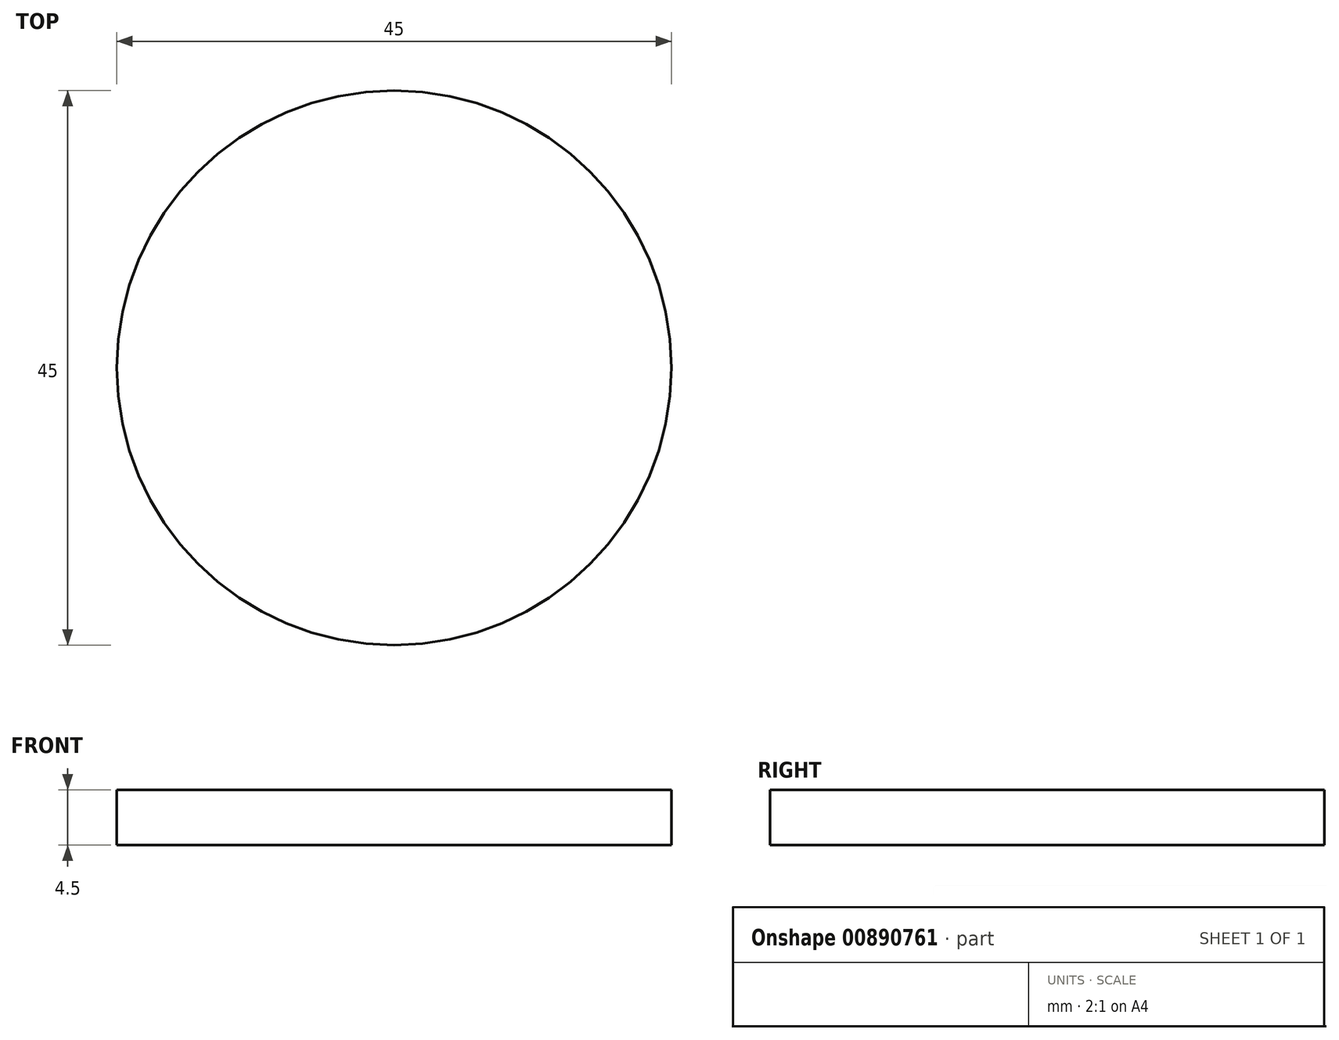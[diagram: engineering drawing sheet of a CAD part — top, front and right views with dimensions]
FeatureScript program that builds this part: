
annotation { "Feature Type Name" : "Feature", "Feature Type Description" : "" }
export const myFeature = defineFeature(function(context is Context, id is Id, definition is map)
    precondition{}
    {
        {
            var Q0;
            Q0=qCreatedBy(makeId("Top.planeOp"),FACE);
            var sketch = newSketch(context, id + "F0", { "sketchPlane" : qUnion([Q0])});
            skCircle(sketch, "E0", {"center": v(0, 0) * mm, "radius": 22.5 * mm});
            skLineSegment(sketch, "E1.left", {"start": v(0, -22.5) * mm, "end": v(0, -20) * mm, "construction": true});
            skLineSegment(sketch, "E2.left", {"start": v(0, -20) * mm, "end": v(0, 26) * mm, "construction": true});
            skEllipse(sketch, "E3", {"center": v(0, 3) * mm, "majorRadius": 23 * mm, "minorRadius": 7 * mm, "majorAxis": v(0, 1)});
            skSolve(sketch);
        }
        {
            var Q0;
            {var subQ0=sQuery(id+"F0.wireOp",EDGE,"E3");var subQ1=sQuery(id+"F0.wireOp",EDGE,"E0");var subQ2=makeQuery(id+"F0.imprint","INTERSECT",VERTEX,{"disambiguationData":[OD(0.0)],"derivedFrom":[subQ1,subQ0]});Q0=makeQuery(id+"F0.imprint","IMPRINT",FACE,{"disambiguationData":[TD([[makeQuery(id+"F0.imprint","IMPRINT",EDGE,{"disambiguationData":[TD([[subQ2,-1.0]])],"derivedFrom":subQ1}),1.0]])]});}
            var Q1;
            {var subQ0=sQuery(id+"F0.wireOp",EDGE,"E3");var subQ1=sQuery(id+"F0.wireOp",EDGE,"E0");var subQ2=makeQuery(id+"F0.imprint","INTERSECT",VERTEX,{"disambiguationData":[OD(0.0)],"derivedFrom":[subQ1,subQ0]});Q1=makeQuery(id+"F0.imprint","IMPRINT",FACE,{"disambiguationData":[TD([[makeQuery(id+"F0.imprint","IMPRINT",EDGE,{"disambiguationData":[TD([[subQ2,1.0]])],"derivedFrom":subQ1}),1.0]])]});}
            extrude(context, id + "F1", {"entities" : qUnion([Q0, Q1]), "depth" : 4.5 * mm, "offsetDistance" : 25 * mm});
        }
    });
